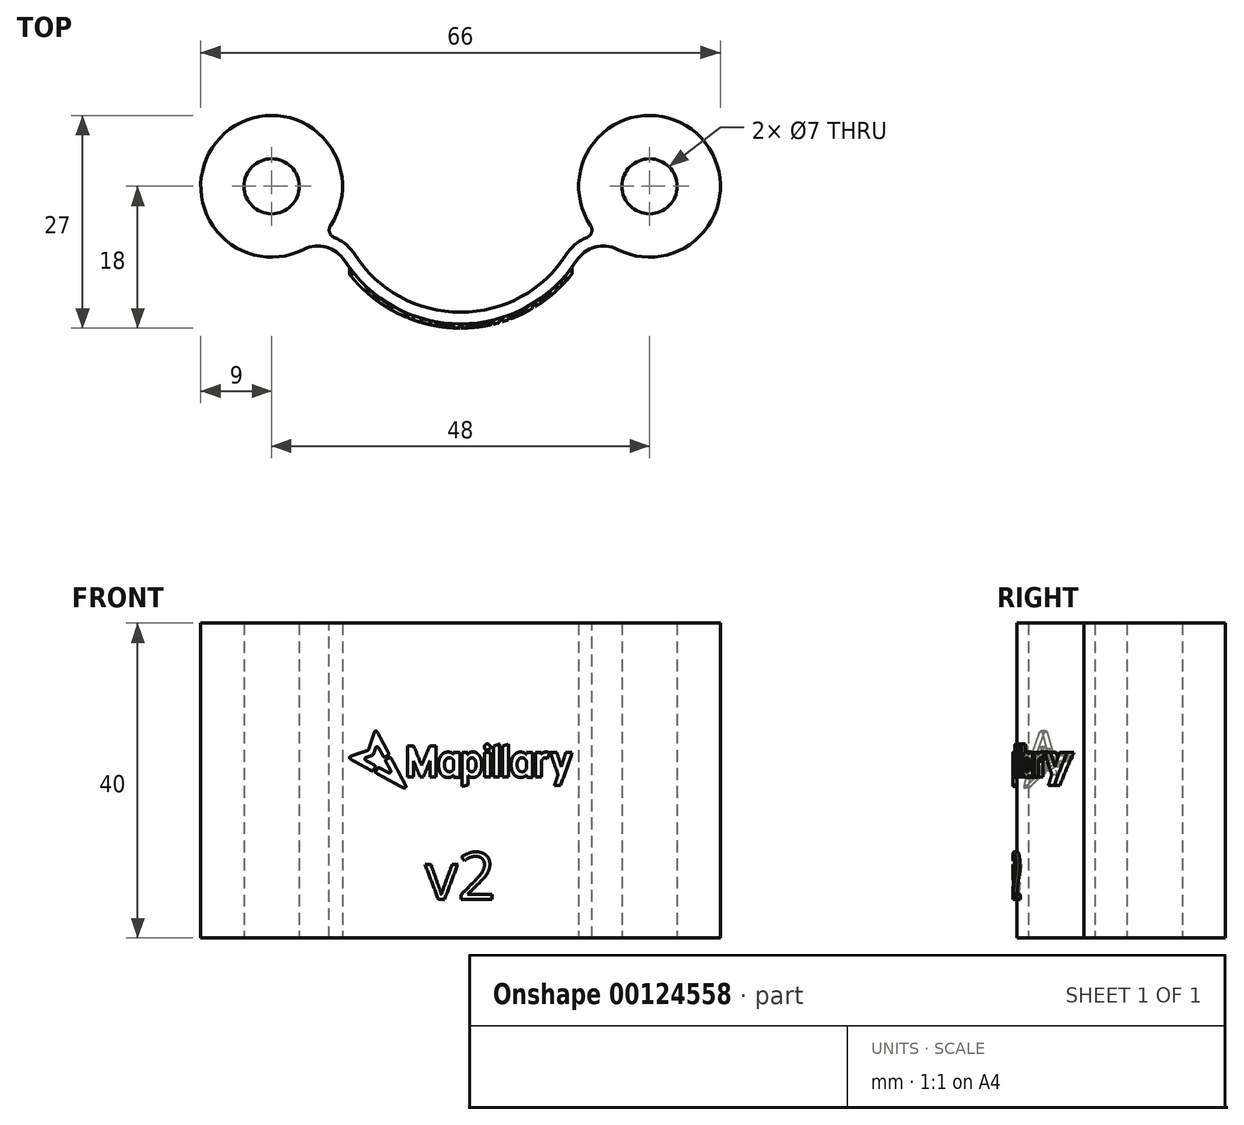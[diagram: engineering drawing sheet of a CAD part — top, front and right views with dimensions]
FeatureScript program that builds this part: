
annotation { "Feature Type Name" : "Feature", "Feature Type Description" : "" }
export const myFeature = defineFeature(function(context is Context, id is Id, definition is map)
    precondition{}
    {
        {
            var Q0;
            Q0=qCreatedBy(makeId("Top.planeOp"),FACE);
            var sketch = newSketch(context, id + "F0", { "sketchPlane" : qUnion([Q0])});
            skCircle(sketch, "E0", {"center": v(-24, 0) * mm, "radius": 3.5 * mm});
            skArc(sketch, "E1", {"start": v(-17.41, -6.13) * mm, "mid": v(-29.42, 7.19) * mm, "end": v(-19.92, -8.02) * mm});
            skArc(sketch, "E2", {"start": v(-13.48, -8.62) * mm, "mid": v(-7.68, -14.04) * mm, "end": v(0, -16) * mm});
            skArc(sketch, "E3", {"start": v(-14.74, -9.43) * mm, "mid": v(-8.4, -15.35) * mm, "end": v(0, -17.5) * mm});
            skArc(sketch, "E4", {"start": v(-14.74, -9.43) * mm, "mid": v(-17.06, -7.73) * mm, "end": v(-19.92, -8.02) * mm});
            skArc(sketch, "E5", {"start": v(-13.48, -8.62) * mm, "mid": v(-15.17, -6.94) * mm, "end": v(-17.41, -6.13) * mm});
            skArc(sketch, "E6.MirrorCS", {"start": v(14.74, -9.43) * mm, "mid": v(17.06, -7.73) * mm, "end": v(19.92, -8.02) * mm});
            skArc(sketch, "E7.MirrorCS", {"start": v(13.48, -8.62) * mm, "mid": v(15.17, -6.94) * mm, "end": v(17.41, -6.13) * mm});
            skCircle(sketch, "E8.MirrorC", {"center": v(24, 0) * mm, "radius": 3.5 * mm});
            skArc(sketch, "E9.MirrorCS", {"start": v(13.48, -8.62) * mm, "mid": v(7.68, -14.04) * mm, "end": v(0, -16) * mm});
            skArc(sketch, "E10.MirrorCS", {"start": v(17.41, -6.13) * mm, "mid": v(29.42, 7.19) * mm, "end": v(19.92, -8.02) * mm});
            skArc(sketch, "E11.MirrorCS", {"start": v(14.74, -9.43) * mm, "mid": v(8.4, -15.35) * mm, "end": v(0, -17.5) * mm});
            skSolve(sketch);
        }
        {
            var Q0;
            Q0 = qSketchRegion(id + "F0", true);
            extrude(context, id + "F1", {"entities" : qUnion([Q0]), "depth" : 40 * mm});
        }
        {
            var Q0;
            Q0=makeQuery(id+"F1.opExtrude","SWEPT_EDGE",EDGE,{"disambiguationData":[OSD([sQuery(id+"F0.wireOp",EDGE,"E1"),sQuery(id+"F0.wireOp",EDGE,"E5")])]});
            var Q1;
            Q1=makeQuery(id+"F1.opExtrude","SWEPT_EDGE",EDGE,{"disambiguationData":[OSD([sQuery(id+"F0.wireOp",EDGE,"E7.MirrorCS"),sQuery(id+"F0.wireOp",EDGE,"E10.MirrorCS")])]});
            fillet(context, id + "F2", {"entities" : qUnion([Q0, Q1]), "radius" : 1 * mm, "tangentPropagation" : true, "allowEdgeOverflow" : false});
        }
        {
            var Q0;
            Q0=qCreatedBy(makeId("Front.planeOp"),FACE);
            cPlane(context, id + "F3", {"entities" : qUnion([Q0]), "cplaneType" : CPlaneType.OFFSET, "offset" : 25 * mm, "width" : 150 * mm, "height" : 150 * mm});
        }
        {
            var Q0;
            Q0=qCreatedBy(id+"F3.planeOp",FACE);
            var sketch = newSketch(context, id + "F4", { "sketchPlane" : qUnion([Q0])});
            skLineSegment(sketch, "E12", {"start": v(-10.66, 20.91) * mm, "end": v(-10.64, 20.9) * mm});
            skLineSegment(sketch, "E13", {"start": v(-10.64, 20.9) * mm, "end": v(-10.6, 20.88) * mm});
            skLineSegment(sketch, "E14", {"start": v(-10.6, 20.88) * mm, "end": v(-10.55, 20.85) * mm});
            skLineSegment(sketch, "E15", {"start": v(-10.55, 20.85) * mm, "end": v(-10.48, 20.82) * mm});
            skLineSegment(sketch, "E16", {"start": v(-10.48, 20.82) * mm, "end": v(-10.4, 20.77) * mm});
            skLineSegment(sketch, "E17", {"start": v(-10.4, 20.77) * mm, "end": v(-10.3, 20.72) * mm});
            skLineSegment(sketch, "E18", {"start": v(-10.3, 20.72) * mm, "end": v(-10.2, 20.67) * mm});
            skLineSegment(sketch, "E19", {"start": v(-10.2, 20.67) * mm, "end": v(-10.09, 20.6) * mm});
            skLineSegment(sketch, "E20", {"start": v(-10.09, 20.6) * mm, "end": v(-9.97, 20.54) * mm});
            skLineSegment(sketch, "E21", {"start": v(-9.97, 20.54) * mm, "end": v(-9.84, 20.47) * mm});
            skLineSegment(sketch, "E22", {"start": v(-9.84, 20.47) * mm, "end": v(-9.7, 20.4) * mm});
            skLineSegment(sketch, "E23", {"start": v(-9.7, 20.4) * mm, "end": v(-9.56, 20.32) * mm});
            skLineSegment(sketch, "E24", {"start": v(-9.56, 20.32) * mm, "end": v(-9.41, 20.24) * mm});
            skLineSegment(sketch, "E25", {"start": v(-9.41, 20.24) * mm, "end": v(-9.26, 20.16) * mm});
            skLineSegment(sketch, "E26", {"start": v(-9.26, 20.16) * mm, "end": v(-9.1, 20.07) * mm});
            skLineSegment(sketch, "E27", {"start": v(-9.1, 20.07) * mm, "end": v(-8.96, 19.99) * mm});
            skLineSegment(sketch, "E28", {"start": v(-8.96, 19.99) * mm, "end": v(-8.8, 19.9) * mm});
            skLineSegment(sketch, "E29", {"start": v(-8.8, 19.9) * mm, "end": v(-8.65, 19.82) * mm});
            skLineSegment(sketch, "E30", {"start": v(-8.65, 19.82) * mm, "end": v(-8.5, 19.74) * mm});
            skLineSegment(sketch, "E31", {"start": v(-8.5, 19.74) * mm, "end": v(-8.36, 19.66) * mm});
            skLineSegment(sketch, "E32", {"start": v(-8.36, 19.66) * mm, "end": v(-8.22, 19.59) * mm});
            skLineSegment(sketch, "E33", {"start": v(-8.22, 19.59) * mm, "end": v(-8.08, 19.51) * mm});
            skLineSegment(sketch, "E34", {"start": v(-8.08, 19.51) * mm, "end": v(-7.95, 19.44) * mm});
            skLineSegment(sketch, "E35", {"start": v(-7.95, 19.44) * mm, "end": v(-7.83, 19.38) * mm});
            skLineSegment(sketch, "E36", {"start": v(-7.83, 19.38) * mm, "end": v(-7.72, 19.32) * mm});
            skLineSegment(sketch, "E37", {"start": v(-7.72, 19.32) * mm, "end": v(-7.62, 19.26) * mm});
            skLineSegment(sketch, "E38", {"start": v(-7.62, 19.26) * mm, "end": v(-7.52, 19.21) * mm});
            skLineSegment(sketch, "E39", {"start": v(-7.52, 19.21) * mm, "end": v(-7.45, 19.17) * mm});
            skLineSegment(sketch, "E40", {"start": v(-7.45, 19.17) * mm, "end": v(-7.38, 19.13) * mm});
            skLineSegment(sketch, "E41", {"start": v(-7.38, 19.13) * mm, "end": v(-7.33, 19.1) * mm});
            skLineSegment(sketch, "E42", {"start": v(-7.33, 19.1) * mm, "end": v(-7.3, 19.09) * mm});
            skLineSegment(sketch, "E43", {"start": v(-7.3, 19.09) * mm, "end": v(-7.28, 19.08) * mm});
            skLineSegment(sketch, "E44", {"start": v(-7.28, 19.08) * mm, "end": v(-7.2, 19.05) * mm});
            skLineSegment(sketch, "E45", {"start": v(-7.2, 19.05) * mm, "end": v(-7.13, 19.05) * mm});
            skLineSegment(sketch, "E46", {"start": v(-7.13, 19.05) * mm, "end": v(-7.07, 19.07) * mm});
            skLineSegment(sketch, "E47", {"start": v(-7.07, 19.07) * mm, "end": v(-7.01, 19.11) * mm});
            skLineSegment(sketch, "E48", {"start": v(-7.01, 19.11) * mm, "end": v(-6.97, 19.17) * mm});
            skLineSegment(sketch, "E49", {"start": v(-6.97, 19.17) * mm, "end": v(-6.95, 19.23) * mm});
            skLineSegment(sketch, "E50", {"start": v(-6.95, 19.23) * mm, "end": v(-6.95, 19.3) * mm});
            skLineSegment(sketch, "E51", {"start": v(-6.95, 19.3) * mm, "end": v(-6.98, 19.38) * mm});
            skLineSegment(sketch, "E52", {"start": v(-6.98, 19.38) * mm, "end": v(-6.99, 19.4) * mm});
            skLineSegment(sketch, "E53", {"start": v(-6.99, 19.4) * mm, "end": v(-7, 19.43) * mm});
            skLineSegment(sketch, "E54", {"start": v(-7, 19.43) * mm, "end": v(-7.03, 19.48) * mm});
            skLineSegment(sketch, "E55", {"start": v(-7.03, 19.48) * mm, "end": v(-7.07, 19.55) * mm});
            skLineSegment(sketch, "E56", {"start": v(-7.07, 19.55) * mm, "end": v(-7.11, 19.63) * mm});
            skLineSegment(sketch, "E57", {"start": v(-7.11, 19.63) * mm, "end": v(-7.16, 19.72) * mm});
            skLineSegment(sketch, "E58", {"start": v(-7.16, 19.72) * mm, "end": v(-7.22, 19.83) * mm});
            skLineSegment(sketch, "E59", {"start": v(-7.22, 19.83) * mm, "end": v(-7.28, 19.94) * mm});
            skLineSegment(sketch, "E60", {"start": v(-7.28, 19.94) * mm, "end": v(-7.34, 20.07) * mm});
            skLineSegment(sketch, "E61", {"start": v(-7.34, 20.07) * mm, "end": v(-7.41, 20.2) * mm});
            skLineSegment(sketch, "E62", {"start": v(-7.41, 20.2) * mm, "end": v(-7.48, 20.34) * mm});
            skLineSegment(sketch, "E63", {"start": v(-7.48, 20.34) * mm, "end": v(-7.56, 20.48) * mm});
            skLineSegment(sketch, "E64", {"start": v(-7.56, 20.48) * mm, "end": v(-7.64, 20.63) * mm});
            skLineSegment(sketch, "E65", {"start": v(-7.64, 20.63) * mm, "end": v(-7.72, 20.78) * mm});
            skLineSegment(sketch, "E66", {"start": v(-7.72, 20.78) * mm, "end": v(-7.8, 20.94) * mm});
            skLineSegment(sketch, "E67", {"start": v(-7.8, 20.94) * mm, "end": v(-7.88, 21.1) * mm});
            skLineSegment(sketch, "E68", {"start": v(-7.88, 21.1) * mm, "end": v(-7.97, 21.25) * mm});
            skLineSegment(sketch, "E69", {"start": v(-7.97, 21.25) * mm, "end": v(-8.05, 21.4) * mm});
            skLineSegment(sketch, "E70", {"start": v(-8.05, 21.4) * mm, "end": v(-8.13, 21.56) * mm});
            skLineSegment(sketch, "E71", {"start": v(-8.13, 21.56) * mm, "end": v(-8.2, 21.7) * mm});
            skLineSegment(sketch, "E72", {"start": v(-8.2, 21.7) * mm, "end": v(-8.29, 21.85) * mm});
            skLineSegment(sketch, "E73", {"start": v(-8.29, 21.85) * mm, "end": v(-8.36, 22) * mm});
            skLineSegment(sketch, "E74", {"start": v(-8.36, 22) * mm, "end": v(-8.43, 22.12) * mm});
            skLineSegment(sketch, "E75", {"start": v(-8.43, 22.12) * mm, "end": v(-8.5, 22.25) * mm});
            skLineSegment(sketch, "E76", {"start": v(-8.5, 22.25) * mm, "end": v(-8.56, 22.36) * mm});
            skLineSegment(sketch, "E77", {"start": v(-8.56, 22.36) * mm, "end": v(-8.61, 22.47) * mm});
            skLineSegment(sketch, "E78", {"start": v(-8.61, 22.47) * mm, "end": v(-8.66, 22.56) * mm});
            skLineSegment(sketch, "E79", {"start": v(-8.66, 22.56) * mm, "end": v(-8.7, 22.64) * mm});
            skLineSegment(sketch, "E80", {"start": v(-8.7, 22.64) * mm, "end": v(-8.74, 22.7) * mm});
            skLineSegment(sketch, "E81", {"start": v(-8.74, 22.7) * mm, "end": v(-8.77, 22.76) * mm});
            skLineSegment(sketch, "E82", {"start": v(-8.77, 22.76) * mm, "end": v(-8.79, 22.8) * mm});
            skLineSegment(sketch, "E83", {"start": v(-8.79, 22.8) * mm, "end": v(-8.8, 22.81) * mm});
            skLineSegment(sketch, "E84", {"start": v(-8.8, 22.81) * mm, "end": v(-8.85, 22.87) * mm});
            skLineSegment(sketch, "E85", {"start": v(-8.85, 22.87) * mm, "end": v(-8.93, 22.91) * mm});
            skLineSegment(sketch, "E86", {"start": v(-8.93, 22.91) * mm, "end": v(-9.02, 22.92) * mm});
            skLineSegment(sketch, "E87", {"start": v(-9.02, 22.92) * mm, "end": v(-9.1, 22.9) * mm});
            skLineSegment(sketch, "E88", {"start": v(-9.1, 22.9) * mm, "end": v(-9.18, 22.84) * mm});
            skLineSegment(sketch, "E89", {"start": v(-9.18, 22.84) * mm, "end": v(-9.26, 22.8) * mm});
            skLineSegment(sketch, "E90", {"start": v(-9.26, 22.8) * mm, "end": v(-9.33, 22.75) * mm});
            skLineSegment(sketch, "E91", {"start": v(-9.33, 22.75) * mm, "end": v(-9.4, 22.72) * mm});
            skLineSegment(sketch, "E92", {"start": v(-9.4, 22.72) * mm, "end": v(-9.47, 22.66) * mm});
            skLineSegment(sketch, "E93", {"start": v(-9.47, 22.66) * mm, "end": v(-9.51, 22.59) * mm});
            skLineSegment(sketch, "E94", {"start": v(-9.51, 22.59) * mm, "end": v(-9.52, 22.5) * mm});
            skLineSegment(sketch, "E95", {"start": v(-9.52, 22.5) * mm, "end": v(-9.48, 22.42) * mm});
            skLineSegment(sketch, "E96", {"start": v(-9.48, 22.42) * mm, "end": v(-9.46, 22.37) * mm});
            skLineSegment(sketch, "E97", {"start": v(-9.46, 22.37) * mm, "end": v(-9.42, 22.3) * mm});
            skLineSegment(sketch, "E98", {"start": v(-9.42, 22.3) * mm, "end": v(-9.38, 22.23) * mm});
            skLineSegment(sketch, "E99", {"start": v(-9.38, 22.23) * mm, "end": v(-9.34, 22.15) * mm});
            skLineSegment(sketch, "E100", {"start": v(-9.34, 22.15) * mm, "end": v(-9.3, 22.06) * mm});
            skLineSegment(sketch, "E101", {"start": v(-9.3, 22.06) * mm, "end": v(-9.25, 21.97) * mm});
            skLineSegment(sketch, "E102", {"start": v(-9.25, 21.97) * mm, "end": v(-9.2, 21.88) * mm});
            skLineSegment(sketch, "E103", {"start": v(-9.2, 21.88) * mm, "end": v(-9.15, 21.79) * mm});
            skLineSegment(sketch, "E104", {"start": v(-9.15, 21.79) * mm, "end": v(-9.1, 21.7) * mm});
            skLineSegment(sketch, "E105", {"start": v(-9.1, 21.7) * mm, "end": v(-9.06, 21.62) * mm});
            skLineSegment(sketch, "E106", {"start": v(-9.06, 21.62) * mm, "end": v(-9.02, 21.54) * mm});
            skLineSegment(sketch, "E107", {"start": v(-9.02, 21.54) * mm, "end": v(-8.98, 21.46) * mm});
            skLineSegment(sketch, "E108", {"start": v(-8.98, 21.46) * mm, "end": v(-8.94, 21.4) * mm});
            skLineSegment(sketch, "E109", {"start": v(-8.94, 21.4) * mm, "end": v(-8.92, 21.35) * mm});
            skLineSegment(sketch, "E110", {"start": v(-8.92, 21.35) * mm, "end": v(-8.9, 21.31) * mm});
            skLineSegment(sketch, "E111", {"start": v(-8.9, 21.31) * mm, "end": v(-8.88, 21.29) * mm});
            skLineSegment(sketch, "E112", {"start": v(-8.88, 21.29) * mm, "end": v(-8.86, 21.22) * mm});
            skLineSegment(sketch, "E113", {"start": v(-8.86, 21.22) * mm, "end": v(-8.86, 21.16) * mm});
            skLineSegment(sketch, "E114", {"start": v(-8.86, 21.16) * mm, "end": v(-8.88, 21.1) * mm});
            skLineSegment(sketch, "E115", {"start": v(-8.88, 21.1) * mm, "end": v(-8.92, 21.05) * mm});
            skLineSegment(sketch, "E116", {"start": v(-8.92, 21.05) * mm, "end": v(-8.98, 21.01) * mm});
            skLineSegment(sketch, "E117", {"start": v(-8.98, 21.01) * mm, "end": v(-9.04, 20.99) * mm});
            skLineSegment(sketch, "E118", {"start": v(-9.04, 20.99) * mm, "end": v(-9.1, 20.98) * mm});
            skLineSegment(sketch, "E119", {"start": v(-9.1, 20.98) * mm, "end": v(-9.16, 21) * mm});
            skLineSegment(sketch, "E120", {"start": v(-9.16, 21) * mm, "end": v(-9.18, 21.02) * mm});
            skLineSegment(sketch, "E121", {"start": v(-9.18, 21.02) * mm, "end": v(-9.22, 21.04) * mm});
            skLineSegment(sketch, "E122", {"start": v(-9.22, 21.04) * mm, "end": v(-9.28, 21.07) * mm});
            skLineSegment(sketch, "E123", {"start": v(-9.28, 21.07) * mm, "end": v(-9.35, 21.11) * mm});
            skLineSegment(sketch, "E124", {"start": v(-9.35, 21.11) * mm, "end": v(-9.44, 21.16) * mm});
            skLineSegment(sketch, "E125", {"start": v(-9.44, 21.16) * mm, "end": v(-9.53, 21.2) * mm});
            skLineSegment(sketch, "E126", {"start": v(-9.53, 21.2) * mm, "end": v(-9.62, 21.26) * mm});
            skLineSegment(sketch, "E127", {"start": v(-9.62, 21.26) * mm, "end": v(-9.72, 21.31) * mm});
            skLineSegment(sketch, "E128", {"start": v(-9.72, 21.31) * mm, "end": v(-9.82, 21.37) * mm});
            skLineSegment(sketch, "E129", {"start": v(-9.82, 21.37) * mm, "end": v(-9.92, 21.42) * mm});
            skLineSegment(sketch, "E130", {"start": v(-9.92, 21.42) * mm, "end": v(-10.01, 21.47) * mm});
            skLineSegment(sketch, "E131", {"start": v(-10.01, 21.47) * mm, "end": v(-10.1, 21.51) * mm});
            skLineSegment(sketch, "E132", {"start": v(-10.1, 21.51) * mm, "end": v(-10.17, 21.55) * mm});
            skLineSegment(sketch, "E133", {"start": v(-10.17, 21.55) * mm, "end": v(-10.23, 21.59) * mm});
            skLineSegment(sketch, "E134", {"start": v(-10.23, 21.59) * mm, "end": v(-10.27, 21.61) * mm});
            skLineSegment(sketch, "E135", {"start": v(-10.27, 21.61) * mm, "end": v(-10.3, 21.62) * mm});
            skLineSegment(sketch, "E136", {"start": v(-10.3, 21.62) * mm, "end": v(-10.36, 21.65) * mm});
            skLineSegment(sketch, "E137", {"start": v(-10.36, 21.65) * mm, "end": v(-10.43, 21.64) * mm});
            skLineSegment(sketch, "E138", {"start": v(-10.43, 21.64) * mm, "end": v(-10.5, 21.6) * mm});
            skLineSegment(sketch, "E139", {"start": v(-10.5, 21.6) * mm, "end": v(-10.58, 21.52) * mm});
            skLineSegment(sketch, "E140", {"start": v(-10.58, 21.52) * mm, "end": v(-10.62, 21.44) * mm});
            skLineSegment(sketch, "E141", {"start": v(-10.62, 21.44) * mm, "end": v(-10.67, 21.36) * mm});
            skLineSegment(sketch, "E142", {"start": v(-10.67, 21.36) * mm, "end": v(-10.72, 21.29) * mm});
            skLineSegment(sketch, "E143", {"start": v(-10.72, 21.29) * mm, "end": v(-10.75, 21.23) * mm});
            skLineSegment(sketch, "E144", {"start": v(-10.75, 21.23) * mm, "end": v(-10.78, 21.13) * mm});
            skLineSegment(sketch, "E145", {"start": v(-10.78, 21.13) * mm, "end": v(-10.78, 21.05) * mm});
            skLineSegment(sketch, "E146", {"start": v(-10.78, 21.05) * mm, "end": v(-10.74, 20.97) * mm});
            skLineSegment(sketch, "E147", {"start": v(-10.74, 20.97) * mm, "end": v(-10.66, 20.91) * mm});
            skLineSegment(sketch, "E148", {"start": v(-13.98, 22.72) * mm, "end": v(-14.04, 22.76) * mm});
            skLineSegment(sketch, "E149", {"start": v(-14.04, 22.76) * mm, "end": v(-14.07, 22.81) * mm});
            skLineSegment(sketch, "E150", {"start": v(-14.07, 22.81) * mm, "end": v(-14.1, 22.87) * mm});
            skLineSegment(sketch, "E151", {"start": v(-14.1, 22.87) * mm, "end": v(-14.09, 22.93) * mm});
            skLineSegment(sketch, "E152", {"start": v(-14.09, 22.93) * mm, "end": v(-14.07, 23) * mm});
            skLineSegment(sketch, "E153", {"start": v(-14.07, 23) * mm, "end": v(-14.03, 23.04) * mm});
            skLineSegment(sketch, "E154", {"start": v(-14.03, 23.04) * mm, "end": v(-13.98, 23.09) * mm});
            skLineSegment(sketch, "E155", {"start": v(-13.98, 23.09) * mm, "end": v(-13.9, 23.12) * mm});
            skLineSegment(sketch, "E156", {"start": v(-13.9, 23.12) * mm, "end": v(-13.86, 23.13) * mm});
            skLineSegment(sketch, "E157", {"start": v(-13.86, 23.13) * mm, "end": v(-13.79, 23.16) * mm});
            skLineSegment(sketch, "E158", {"start": v(-13.79, 23.16) * mm, "end": v(-13.69, 23.2) * mm});
            skLineSegment(sketch, "E159", {"start": v(-13.69, 23.2) * mm, "end": v(-13.57, 23.23) * mm});
            skLineSegment(sketch, "E160", {"start": v(-13.57, 23.23) * mm, "end": v(-13.44, 23.28) * mm});
            skLineSegment(sketch, "E161", {"start": v(-13.44, 23.28) * mm, "end": v(-13.3, 23.33) * mm});
            skLineSegment(sketch, "E162", {"start": v(-13.3, 23.33) * mm, "end": v(-13.13, 23.38) * mm});
            skLineSegment(sketch, "E163", {"start": v(-13.13, 23.38) * mm, "end": v(-12.97, 23.44) * mm});
            skLineSegment(sketch, "E164", {"start": v(-12.97, 23.44) * mm, "end": v(-12.8, 23.5) * mm});
            skLineSegment(sketch, "E165", {"start": v(-12.8, 23.5) * mm, "end": v(-12.64, 23.55) * mm});
            skLineSegment(sketch, "E166", {"start": v(-12.64, 23.55) * mm, "end": v(-12.47, 23.6) * mm});
            skLineSegment(sketch, "E167", {"start": v(-12.47, 23.6) * mm, "end": v(-12.32, 23.66) * mm});
            skLineSegment(sketch, "E168", {"start": v(-12.32, 23.66) * mm, "end": v(-12.17, 23.7) * mm});
            skLineSegment(sketch, "E169", {"start": v(-12.17, 23.7) * mm, "end": v(-12.04, 23.75) * mm});
            skLineSegment(sketch, "E170", {"start": v(-12.04, 23.75) * mm, "end": v(-11.93, 23.8) * mm});
            skLineSegment(sketch, "E171", {"start": v(-11.93, 23.8) * mm, "end": v(-11.83, 23.83) * mm});
            skLineSegment(sketch, "E172", {"start": v(-11.83, 23.83) * mm, "end": v(-11.78, 23.85) * mm});
            skLineSegment(sketch, "E173", {"start": v(-11.78, 23.85) * mm, "end": v(-11.73, 23.9) * mm});
            skLineSegment(sketch, "E174", {"start": v(-11.73, 23.9) * mm, "end": v(-11.7, 23.94) * mm});
            skLineSegment(sketch, "E175", {"start": v(-11.7, 23.94) * mm, "end": v(-11.67, 24) * mm});
            skLineSegment(sketch, "E176", {"start": v(-11.67, 24) * mm, "end": v(-11.63, 24.1) * mm});
            skLineSegment(sketch, "E177", {"start": v(-11.63, 24.1) * mm, "end": v(-11.6, 24.21) * mm});
            skLineSegment(sketch, "E178", {"start": v(-11.6, 24.21) * mm, "end": v(-11.55, 24.35) * mm});
            skLineSegment(sketch, "E179", {"start": v(-11.55, 24.35) * mm, "end": v(-11.5, 24.5) * mm});
            skLineSegment(sketch, "E180", {"start": v(-11.5, 24.5) * mm, "end": v(-11.45, 24.66) * mm});
            skLineSegment(sketch, "E181", {"start": v(-11.45, 24.66) * mm, "end": v(-11.4, 24.83) * mm});
            skLineSegment(sketch, "E182", {"start": v(-11.4, 24.83) * mm, "end": v(-11.33, 25) * mm});
            skLineSegment(sketch, "E183", {"start": v(-11.33, 25) * mm, "end": v(-11.28, 25.17) * mm});
            skLineSegment(sketch, "E184", {"start": v(-11.28, 25.17) * mm, "end": v(-11.22, 25.34) * mm});
            skLineSegment(sketch, "E185", {"start": v(-11.22, 25.34) * mm, "end": v(-11.17, 25.5) * mm});
            skLineSegment(sketch, "E186", {"start": v(-11.17, 25.5) * mm, "end": v(-11.12, 25.65) * mm});
            skLineSegment(sketch, "E187", {"start": v(-11.12, 25.65) * mm, "end": v(-11.07, 25.8) * mm});
            skLineSegment(sketch, "E188", {"start": v(-11.07, 25.8) * mm, "end": v(-11.03, 25.91) * mm});
            skLineSegment(sketch, "E189", {"start": v(-11.03, 25.91) * mm, "end": v(-11, 26) * mm});
            skLineSegment(sketch, "E190", {"start": v(-11, 26) * mm, "end": v(-10.97, 26.08) * mm});
            skLineSegment(sketch, "E191", {"start": v(-10.97, 26.08) * mm, "end": v(-10.96, 26.13) * mm});
            skLineSegment(sketch, "E192", {"start": v(-10.96, 26.13) * mm, "end": v(-10.93, 26.2) * mm});
            skLineSegment(sketch, "E193", {"start": v(-10.93, 26.2) * mm, "end": v(-10.88, 26.24) * mm});
            skLineSegment(sketch, "E194", {"start": v(-10.88, 26.24) * mm, "end": v(-10.83, 26.27) * mm});
            skLineSegment(sketch, "E195", {"start": v(-10.83, 26.27) * mm, "end": v(-10.77, 26.28) * mm});
            skLineSegment(sketch, "E196", {"start": v(-10.77, 26.28) * mm, "end": v(-10.7, 26.27) * mm});
            skLineSegment(sketch, "E197", {"start": v(-10.7, 26.27) * mm, "end": v(-10.65, 26.25) * mm});
            skLineSegment(sketch, "E198", {"start": v(-10.65, 26.25) * mm, "end": v(-10.6, 26.2) * mm});
            skLineSegment(sketch, "E199", {"start": v(-10.6, 26.2) * mm, "end": v(-10.55, 26.14) * mm});
            skLineSegment(sketch, "E200", {"start": v(-10.55, 26.14) * mm, "end": v(-10.53, 26.1) * mm});
            skLineSegment(sketch, "E201", {"start": v(-10.53, 26.1) * mm, "end": v(-10.49, 26.01) * mm});
            skLineSegment(sketch, "E202", {"start": v(-10.49, 26.01) * mm, "end": v(-10.42, 25.88) * mm});
            skLineSegment(sketch, "E203", {"start": v(-10.42, 25.88) * mm, "end": v(-10.33, 25.71) * mm});
            skLineSegment(sketch, "E204", {"start": v(-10.33, 25.71) * mm, "end": v(-10.22, 25.52) * mm});
            skLineSegment(sketch, "E205", {"start": v(-10.22, 25.52) * mm, "end": v(-10.1, 25.3) * mm});
            skLineSegment(sketch, "E206", {"start": v(-10.1, 25.3) * mm, "end": v(-9.99, 25.07) * mm});
            skLineSegment(sketch, "E207", {"start": v(-9.99, 25.07) * mm, "end": v(-9.86, 24.84) * mm});
            skLineSegment(sketch, "E208", {"start": v(-9.86, 24.84) * mm, "end": v(-9.73, 24.6) * mm});
            skLineSegment(sketch, "E209", {"start": v(-9.73, 24.6) * mm, "end": v(-9.6, 24.37) * mm});
            skLineSegment(sketch, "E210", {"start": v(-9.6, 24.37) * mm, "end": v(-9.5, 24.15) * mm});
            skLineSegment(sketch, "E211", {"start": v(-9.5, 24.15) * mm, "end": v(-9.39, 23.95) * mm});
            skLineSegment(sketch, "E212", {"start": v(-9.39, 23.95) * mm, "end": v(-9.3, 23.78) * mm});
            skLineSegment(sketch, "E213", {"start": v(-9.3, 23.78) * mm, "end": v(-9.23, 23.65) * mm});
            skLineSegment(sketch, "E214", {"start": v(-9.23, 23.65) * mm, "end": v(-9.18, 23.55) * mm});
            skLineSegment(sketch, "E215", {"start": v(-9.18, 23.55) * mm, "end": v(-9.15, 23.5) * mm});
            skLineSegment(sketch, "E216", {"start": v(-9.15, 23.5) * mm, "end": v(-9.13, 23.43) * mm});
            skLineSegment(sketch, "E217", {"start": v(-9.13, 23.43) * mm, "end": v(-9.14, 23.35) * mm});
            skLineSegment(sketch, "E218", {"start": v(-9.14, 23.35) * mm, "end": v(-9.18, 23.28) * mm});
            skLineSegment(sketch, "E219", {"start": v(-9.18, 23.28) * mm, "end": v(-9.24, 23.22) * mm});
            skLineSegment(sketch, "E220", {"start": v(-9.24, 23.22) * mm, "end": v(-9.33, 23.17) * mm});
            skLineSegment(sketch, "E221", {"start": v(-9.33, 23.17) * mm, "end": v(-9.43, 23.1) * mm});
            skLineSegment(sketch, "E222", {"start": v(-9.43, 23.1) * mm, "end": v(-9.51, 23.06) * mm});
            skLineSegment(sketch, "E223", {"start": v(-9.51, 23.06) * mm, "end": v(-9.58, 23.02) * mm});
            skLineSegment(sketch, "E224", {"start": v(-9.58, 23.02) * mm, "end": v(-9.65, 22.99) * mm});
            skLineSegment(sketch, "E225", {"start": v(-9.65, 22.99) * mm, "end": v(-9.73, 23) * mm});
            skLineSegment(sketch, "E226", {"start": v(-9.73, 23) * mm, "end": v(-9.79, 23.04) * mm});
            skLineSegment(sketch, "E227", {"start": v(-9.79, 23.04) * mm, "end": v(-9.83, 23.1) * mm});
            skLineSegment(sketch, "E228", {"start": v(-9.83, 23.1) * mm, "end": v(-9.87, 23.17) * mm});
            skLineSegment(sketch, "E229", {"start": v(-9.87, 23.17) * mm, "end": v(-9.92, 23.28) * mm});
            skLineSegment(sketch, "E230", {"start": v(-9.92, 23.28) * mm, "end": v(-10, 23.41) * mm});
            skLineSegment(sketch, "E231", {"start": v(-10, 23.41) * mm, "end": v(-10.08, 23.57) * mm});
            skLineSegment(sketch, "E232", {"start": v(-10.08, 23.57) * mm, "end": v(-10.17, 23.74) * mm});
            skLineSegment(sketch, "E233", {"start": v(-10.17, 23.74) * mm, "end": v(-10.26, 23.9) * mm});
            skLineSegment(sketch, "E234", {"start": v(-10.26, 23.9) * mm, "end": v(-10.35, 24.06) * mm});
            skLineSegment(sketch, "E235", {"start": v(-10.35, 24.06) * mm, "end": v(-10.41, 24.18) * mm});
            skLineSegment(sketch, "E236", {"start": v(-10.41, 24.18) * mm, "end": v(-10.45, 24.23) * mm});
            skLineSegment(sketch, "E237", {"start": v(-10.45, 24.23) * mm, "end": v(-10.5, 24.27) * mm});
            skLineSegment(sketch, "E238", {"start": v(-10.5, 24.27) * mm, "end": v(-10.55, 24.3) * mm});
            skLineSegment(sketch, "E239", {"start": v(-10.55, 24.3) * mm, "end": v(-10.6, 24.3) * mm});
            skLineSegment(sketch, "E240", {"start": v(-10.6, 24.3) * mm, "end": v(-10.66, 24.3) * mm});
            skLineSegment(sketch, "E241", {"start": v(-10.66, 24.3) * mm, "end": v(-10.72, 24.27) * mm});
            skLineSegment(sketch, "E242", {"start": v(-10.72, 24.27) * mm, "end": v(-10.76, 24.22) * mm});
            skLineSegment(sketch, "E243", {"start": v(-10.76, 24.22) * mm, "end": v(-10.8, 24.15) * mm});
            skLineSegment(sketch, "E244", {"start": v(-10.8, 24.15) * mm, "end": v(-10.82, 24.07) * mm});
            skLineSegment(sketch, "E245", {"start": v(-10.82, 24.07) * mm, "end": v(-10.85, 23.99) * mm});
            skLineSegment(sketch, "E246", {"start": v(-10.85, 23.99) * mm, "end": v(-10.88, 23.88) * mm});
            skLineSegment(sketch, "E247", {"start": v(-10.88, 23.88) * mm, "end": v(-10.92, 23.78) * mm});
            skLineSegment(sketch, "E248", {"start": v(-10.92, 23.78) * mm, "end": v(-10.96, 23.67) * mm});
            skLineSegment(sketch, "E249", {"start": v(-10.96, 23.67) * mm, "end": v(-11, 23.56) * mm});
            skLineSegment(sketch, "E250", {"start": v(-11, 23.56) * mm, "end": v(-11.02, 23.46) * mm});
            skLineSegment(sketch, "E251", {"start": v(-11.02, 23.46) * mm, "end": v(-11.05, 23.38) * mm});
            skLineSegment(sketch, "E252", {"start": v(-11.05, 23.38) * mm, "end": v(-11.08, 23.32) * mm});
            skLineSegment(sketch, "E253", {"start": v(-11.08, 23.32) * mm, "end": v(-11.12, 23.27) * mm});
            skLineSegment(sketch, "E254", {"start": v(-11.12, 23.27) * mm, "end": v(-11.17, 23.23) * mm});
            skLineSegment(sketch, "E255", {"start": v(-11.17, 23.23) * mm, "end": v(-11.22, 23.2) * mm});
            skLineSegment(sketch, "E256", {"start": v(-11.22, 23.2) * mm, "end": v(-11.3, 23.18) * mm});
            skLineSegment(sketch, "E257", {"start": v(-11.3, 23.18) * mm, "end": v(-11.4, 23.15) * mm});
            skLineSegment(sketch, "E258", {"start": v(-11.4, 23.15) * mm, "end": v(-11.5, 23.11) * mm});
            skLineSegment(sketch, "E259", {"start": v(-11.5, 23.11) * mm, "end": v(-11.6, 23.08) * mm});
            skLineSegment(sketch, "E260", {"start": v(-11.6, 23.08) * mm, "end": v(-11.7, 23.04) * mm});
            skLineSegment(sketch, "E261", {"start": v(-11.7, 23.04) * mm, "end": v(-11.8, 23) * mm});
            skLineSegment(sketch, "E262", {"start": v(-11.8, 23) * mm, "end": v(-11.9, 22.97) * mm});
            skLineSegment(sketch, "E263", {"start": v(-11.9, 22.97) * mm, "end": v(-11.99, 22.94) * mm});
            skLineSegment(sketch, "E264", {"start": v(-11.99, 22.94) * mm, "end": v(-12.04, 22.92) * mm});
            skLineSegment(sketch, "E265", {"start": v(-12.04, 22.92) * mm, "end": v(-12.09, 22.88) * mm});
            skLineSegment(sketch, "E266", {"start": v(-12.09, 22.88) * mm, "end": v(-12.12, 22.82) * mm});
            skLineSegment(sketch, "E267", {"start": v(-12.12, 22.82) * mm, "end": v(-12.13, 22.77) * mm});
            skLineSegment(sketch, "E268", {"start": v(-12.13, 22.77) * mm, "end": v(-12.13, 22.7) * mm});
            skLineSegment(sketch, "E269", {"start": v(-12.13, 22.7) * mm, "end": v(-12.11, 22.65) * mm});
            skLineSegment(sketch, "E270", {"start": v(-12.11, 22.65) * mm, "end": v(-12.07, 22.6) * mm});
            skLineSegment(sketch, "E271", {"start": v(-12.07, 22.6) * mm, "end": v(-12.01, 22.55) * mm});
            skLineSegment(sketch, "E272", {"start": v(-12.01, 22.55) * mm, "end": v(-12, 22.54) * mm});
            skLineSegment(sketch, "E273", {"start": v(-12, 22.54) * mm, "end": v(-11.96, 22.52) * mm});
            skLineSegment(sketch, "E274", {"start": v(-11.96, 22.52) * mm, "end": v(-11.9, 22.5) * mm});
            skLineSegment(sketch, "E275", {"start": v(-11.9, 22.5) * mm, "end": v(-11.84, 22.46) * mm});
            skLineSegment(sketch, "E276", {"start": v(-11.84, 22.46) * mm, "end": v(-11.76, 22.42) * mm});
            skLineSegment(sketch, "E277", {"start": v(-11.76, 22.42) * mm, "end": v(-11.68, 22.37) * mm});
            skLineSegment(sketch, "E278", {"start": v(-11.68, 22.37) * mm, "end": v(-11.6, 22.33) * mm});
            skLineSegment(sketch, "E279", {"start": v(-11.6, 22.33) * mm, "end": v(-11.5, 22.27) * mm});
            skLineSegment(sketch, "E280", {"start": v(-11.5, 22.27) * mm, "end": v(-11.4, 22.22) * mm});
            skLineSegment(sketch, "E281", {"start": v(-11.4, 22.22) * mm, "end": v(-11.32, 22.17) * mm});
            skLineSegment(sketch, "E282", {"start": v(-11.32, 22.17) * mm, "end": v(-11.23, 22.13) * mm});
            skLineSegment(sketch, "E283", {"start": v(-11.23, 22.13) * mm, "end": v(-11.15, 22.08) * mm});
            skLineSegment(sketch, "E284", {"start": v(-11.15, 22.08) * mm, "end": v(-11.08, 22.05) * mm});
            skLineSegment(sketch, "E285", {"start": v(-11.08, 22.05) * mm, "end": v(-11.02, 22.01) * mm});
            skLineSegment(sketch, "E286", {"start": v(-11.02, 22.01) * mm, "end": v(-10.98, 22) * mm});
            skLineSegment(sketch, "E287", {"start": v(-10.98, 22) * mm, "end": v(-10.95, 21.98) * mm});
            skLineSegment(sketch, "E288", {"start": v(-10.95, 21.98) * mm, "end": v(-10.89, 21.93) * mm});
            skLineSegment(sketch, "E289", {"start": v(-10.89, 21.93) * mm, "end": v(-10.85, 21.86) * mm});
            skLineSegment(sketch, "E290", {"start": v(-10.85, 21.86) * mm, "end": v(-10.84, 21.78) * mm});
            skLineSegment(sketch, "E291", {"start": v(-10.84, 21.78) * mm, "end": v(-10.86, 21.7) * mm});
            skLineSegment(sketch, "E292", {"start": v(-10.86, 21.7) * mm, "end": v(-10.92, 21.6) * mm});
            skLineSegment(sketch, "E293", {"start": v(-10.92, 21.6) * mm, "end": v(-10.98, 21.5) * mm});
            skLineSegment(sketch, "E294", {"start": v(-10.98, 21.5) * mm, "end": v(-11.03, 21.41) * mm});
            skLineSegment(sketch, "E295", {"start": v(-11.03, 21.41) * mm, "end": v(-11.07, 21.35) * mm});
            skLineSegment(sketch, "E296", {"start": v(-11.07, 21.35) * mm, "end": v(-11.12, 21.3) * mm});
            skLineSegment(sketch, "E297", {"start": v(-11.12, 21.3) * mm, "end": v(-11.2, 21.26) * mm});
            skLineSegment(sketch, "E298", {"start": v(-11.2, 21.26) * mm, "end": v(-11.27, 21.26) * mm});
            skLineSegment(sketch, "E299", {"start": v(-11.27, 21.26) * mm, "end": v(-11.35, 21.28) * mm});
            skLineSegment(sketch, "E300", {"start": v(-11.35, 21.28) * mm, "end": v(-11.37, 21.3) * mm});
            skLineSegment(sketch, "E301", {"start": v(-11.37, 21.3) * mm, "end": v(-11.4, 21.3) * mm});
            skLineSegment(sketch, "E302", {"start": v(-11.4, 21.3) * mm, "end": v(-11.44, 21.33) * mm});
            skLineSegment(sketch, "E303", {"start": v(-11.44, 21.33) * mm, "end": v(-11.49, 21.36) * mm});
            skLineSegment(sketch, "E304", {"start": v(-11.49, 21.36) * mm, "end": v(-11.55, 21.4) * mm});
            skLineSegment(sketch, "E305", {"start": v(-11.55, 21.4) * mm, "end": v(-11.62, 21.43) * mm});
            skLineSegment(sketch, "E306", {"start": v(-11.62, 21.43) * mm, "end": v(-11.7, 21.48) * mm});
            skLineSegment(sketch, "E307", {"start": v(-11.7, 21.48) * mm, "end": v(-11.8, 21.53) * mm});
            skLineSegment(sketch, "E308", {"start": v(-11.8, 21.53) * mm, "end": v(-11.9, 21.58) * mm});
            skLineSegment(sketch, "E309", {"start": v(-11.9, 21.58) * mm, "end": v(-12, 21.64) * mm});
            skLineSegment(sketch, "E310", {"start": v(-12, 21.64) * mm, "end": v(-12.1, 21.7) * mm});
            skLineSegment(sketch, "E311", {"start": v(-12.1, 21.7) * mm, "end": v(-12.21, 21.75) * mm});
            skLineSegment(sketch, "E312", {"start": v(-12.21, 21.75) * mm, "end": v(-12.33, 21.82) * mm});
            skLineSegment(sketch, "E313", {"start": v(-12.33, 21.82) * mm, "end": v(-12.44, 21.88) * mm});
            skLineSegment(sketch, "E314", {"start": v(-12.44, 21.88) * mm, "end": v(-12.56, 21.95) * mm});
            skLineSegment(sketch, "E315", {"start": v(-12.56, 21.95) * mm, "end": v(-12.68, 22.01) * mm});
            skLineSegment(sketch, "E316", {"start": v(-12.68, 22.01) * mm, "end": v(-12.8, 22.08) * mm});
            skLineSegment(sketch, "E317", {"start": v(-12.8, 22.08) * mm, "end": v(-12.92, 22.14) * mm});
            skLineSegment(sketch, "E318", {"start": v(-12.92, 22.14) * mm, "end": v(-13.04, 22.2) * mm});
            skLineSegment(sketch, "E319", {"start": v(-13.04, 22.2) * mm, "end": v(-13.15, 22.27) * mm});
            skLineSegment(sketch, "E320", {"start": v(-13.15, 22.27) * mm, "end": v(-13.26, 22.33) * mm});
            skLineSegment(sketch, "E321", {"start": v(-13.26, 22.33) * mm, "end": v(-13.37, 22.38) * mm});
            skLineSegment(sketch, "E322", {"start": v(-13.37, 22.38) * mm, "end": v(-13.47, 22.44) * mm});
            skLineSegment(sketch, "E323", {"start": v(-13.47, 22.44) * mm, "end": v(-13.56, 22.5) * mm});
            skLineSegment(sketch, "E324", {"start": v(-13.56, 22.5) * mm, "end": v(-13.65, 22.54) * mm});
            skLineSegment(sketch, "E325", {"start": v(-13.65, 22.54) * mm, "end": v(-13.73, 22.58) * mm});
            skLineSegment(sketch, "E326", {"start": v(-13.73, 22.58) * mm, "end": v(-13.8, 22.62) * mm});
            skLineSegment(sketch, "E327", {"start": v(-13.8, 22.62) * mm, "end": v(-13.86, 22.65) * mm});
            skLineSegment(sketch, "E328", {"start": v(-13.86, 22.65) * mm, "end": v(-13.9, 22.68) * mm});
            skLineSegment(sketch, "E329", {"start": v(-13.9, 22.68) * mm, "end": v(-13.95, 22.7) * mm});
            skLineSegment(sketch, "E330", {"start": v(-13.95, 22.7) * mm, "end": v(-13.97, 22.71) * mm});
            skLineSegment(sketch, "E331", {"start": v(-13.97, 22.71) * mm, "end": v(-13.98, 22.72) * mm});
            skLineSegment(sketch, "E332", {"start": v(-3.11, 24.43) * mm, "end": v(-3.11, 20.47) * mm});
            skLineSegment(sketch, "E333", {"start": v(-3.11, 20.47) * mm, "end": v(-3.87, 20.47) * mm});
            skLineSegment(sketch, "E334", {"start": v(-3.87, 20.47) * mm, "end": v(-3.87, 22.53) * mm});
            skLineSegment(sketch, "E335", {"start": v(-3.87, 22.53) * mm, "end": v(-4.73, 20.47) * mm});
            skLineSegment(sketch, "E336", {"start": v(-4.73, 20.47) * mm, "end": v(-5.14, 20.47) * mm});
            skLineSegment(sketch, "E337", {"start": v(-5.14, 20.47) * mm, "end": v(-6, 22.53) * mm});
            skLineSegment(sketch, "E338", {"start": v(-6, 22.53) * mm, "end": v(-6, 20.47) * mm});
            skLineSegment(sketch, "E339", {"start": v(-6, 20.47) * mm, "end": v(-6.76, 20.47) * mm});
            skLineSegment(sketch, "E340", {"start": v(-6.76, 20.47) * mm, "end": v(-6.76, 24.43) * mm});
            skLineSegment(sketch, "E341", {"start": v(-6.76, 24.43) * mm, "end": v(-5.98, 24.43) * mm});
            skLineSegment(sketch, "E342", {"start": v(-5.98, 24.43) * mm, "end": v(-4.94, 21.94) * mm});
            skLineSegment(sketch, "E343", {"start": v(-4.94, 21.94) * mm, "end": v(-3.9, 24.43) * mm});
            skLineSegment(sketch, "E344", {"start": v(-3.9, 24.43) * mm, "end": v(-3.11, 24.43) * mm});
            skLineSegment(sketch, "E345", {"start": v(0.2, 23.57) * mm, "end": v(0.88, 23.57) * mm});
            skLineSegment(sketch, "E346", {"start": v(0.88, 23.57) * mm, "end": v(0.88, 23.3) * mm});
            skLineSegment(sketch, "E347", {"start": v(0.88, 23.3) * mm, "end": v(0.92, 23.38) * mm});
            skLineSegment(sketch, "E348", {"start": v(0.92, 23.38) * mm, "end": v(0.98, 23.44) * mm});
            skLineSegment(sketch, "E349", {"start": v(0.98, 23.44) * mm, "end": v(1.05, 23.5) * mm});
            skLineSegment(sketch, "E350", {"start": v(1.05, 23.5) * mm, "end": v(1.14, 23.54) * mm});
            skLineSegment(sketch, "E351", {"start": v(1.14, 23.54) * mm, "end": v(1.36, 23.62) * mm});
            skLineSegment(sketch, "E352", {"start": v(1.36, 23.62) * mm, "end": v(1.59, 23.64) * mm});
            skLineSegment(sketch, "E353", {"start": v(1.59, 23.64) * mm, "end": v(1.8, 23.62) * mm});
            skLineSegment(sketch, "E354", {"start": v(1.8, 23.62) * mm, "end": v(2.02, 23.54) * mm});
            skLineSegment(sketch, "E355", {"start": v(2.02, 23.54) * mm, "end": v(2.2, 23.4) * mm});
            skLineSegment(sketch, "E356", {"start": v(2.2, 23.4) * mm, "end": v(2.37, 23.22) * mm});
            skLineSegment(sketch, "E357", {"start": v(2.37, 23.22) * mm, "end": v(2.5, 23) * mm});
            skLineSegment(sketch, "E358", {"start": v(2.5, 23) * mm, "end": v(2.6, 22.71) * mm});
            skLineSegment(sketch, "E359", {"start": v(2.6, 22.71) * mm, "end": v(2.67, 22.39) * mm});
            skLineSegment(sketch, "E360", {"start": v(2.67, 22.39) * mm, "end": v(2.69, 22.02) * mm});
            skLineSegment(sketch, "E361", {"start": v(2.69, 22.02) * mm, "end": v(2.68, 21.83) * mm});
            skLineSegment(sketch, "E362", {"start": v(2.68, 21.83) * mm, "end": v(2.67, 21.65) * mm});
            skLineSegment(sketch, "E363", {"start": v(2.67, 21.65) * mm, "end": v(2.64, 21.48) * mm});
            skLineSegment(sketch, "E364", {"start": v(2.64, 21.48) * mm, "end": v(2.6, 21.32) * mm});
            skLineSegment(sketch, "E365", {"start": v(2.6, 21.32) * mm, "end": v(2.5, 21.04) * mm});
            skLineSegment(sketch, "E366", {"start": v(2.5, 21.04) * mm, "end": v(2.38, 20.8) * mm});
            skLineSegment(sketch, "E367", {"start": v(2.38, 20.8) * mm, "end": v(2.22, 20.63) * mm});
            skLineSegment(sketch, "E368", {"start": v(2.22, 20.63) * mm, "end": v(2.03, 20.5) * mm});
            skLineSegment(sketch, "E369", {"start": v(2.03, 20.5) * mm, "end": v(1.82, 20.42) * mm});
            skLineSegment(sketch, "E370", {"start": v(1.82, 20.42) * mm, "end": v(1.6, 20.4) * mm});
            skLineSegment(sketch, "E371", {"start": v(1.6, 20.4) * mm, "end": v(1.48, 20.4) * mm});
            skLineSegment(sketch, "E372", {"start": v(1.48, 20.4) * mm, "end": v(1.37, 20.42) * mm});
            skLineSegment(sketch, "E373", {"start": v(1.37, 20.42) * mm, "end": v(1.27, 20.44) * mm});
            skLineSegment(sketch, "E374", {"start": v(1.27, 20.44) * mm, "end": v(1.2, 20.48) * mm});
            skLineSegment(sketch, "E375", {"start": v(1.2, 20.48) * mm, "end": v(1.06, 20.57) * mm});
            skLineSegment(sketch, "E376", {"start": v(1.06, 20.57) * mm, "end": v(0.97, 20.68) * mm});
            skLineSegment(sketch, "E377", {"start": v(0.97, 20.68) * mm, "end": v(0.97, 19.44) * mm});
            skLineSegment(sketch, "E378", {"start": v(0.97, 19.44) * mm, "end": v(0.2, 19.28) * mm});
            skLineSegment(sketch, "E379", {"start": v(0.2, 19.28) * mm, "end": v(0.2, 23.57) * mm});
            skLineSegment(sketch, "E380", {"start": v(1.4, 21.14) * mm, "end": v(1.54, 21.15) * mm});
            skLineSegment(sketch, "E381", {"start": v(1.54, 21.15) * mm, "end": v(1.65, 21.2) * mm});
            skLineSegment(sketch, "E382", {"start": v(1.65, 21.2) * mm, "end": v(1.74, 21.26) * mm});
            skLineSegment(sketch, "E383", {"start": v(1.74, 21.26) * mm, "end": v(1.82, 21.36) * mm});
            skLineSegment(sketch, "E384", {"start": v(1.82, 21.36) * mm, "end": v(1.88, 21.48) * mm});
            skLineSegment(sketch, "E385", {"start": v(1.88, 21.48) * mm, "end": v(1.93, 21.63) * mm});
            skLineSegment(sketch, "E386", {"start": v(1.93, 21.63) * mm, "end": v(1.95, 21.8) * mm});
            skLineSegment(sketch, "E387", {"start": v(1.95, 21.8) * mm, "end": v(1.96, 22.02) * mm});
            skLineSegment(sketch, "E388", {"start": v(1.96, 22.02) * mm, "end": v(1.95, 22.22) * mm});
            skLineSegment(sketch, "E389", {"start": v(1.95, 22.22) * mm, "end": v(1.93, 22.4) * mm});
            skLineSegment(sketch, "E390", {"start": v(1.93, 22.4) * mm, "end": v(1.88, 22.54) * mm});
            skLineSegment(sketch, "E391", {"start": v(1.88, 22.54) * mm, "end": v(1.82, 22.67) * mm});
            skLineSegment(sketch, "E392", {"start": v(1.82, 22.67) * mm, "end": v(1.75, 22.77) * mm});
            skLineSegment(sketch, "E393", {"start": v(1.75, 22.77) * mm, "end": v(1.66, 22.84) * mm});
            skLineSegment(sketch, "E394", {"start": v(1.66, 22.84) * mm, "end": v(1.55, 22.88) * mm});
            skLineSegment(sketch, "E395", {"start": v(1.55, 22.88) * mm, "end": v(1.43, 22.9) * mm});
            skLineSegment(sketch, "E396", {"start": v(1.43, 22.9) * mm, "end": v(1.34, 22.88) * mm});
            skLineSegment(sketch, "E397", {"start": v(1.34, 22.88) * mm, "end": v(1.26, 22.86) * mm});
            skLineSegment(sketch, "E398", {"start": v(1.26, 22.86) * mm, "end": v(1.18, 22.82) * mm});
            skLineSegment(sketch, "E399", {"start": v(1.18, 22.82) * mm, "end": v(1.11, 22.76) * mm});
            skLineSegment(sketch, "E400", {"start": v(1.11, 22.76) * mm, "end": v(1, 22.61) * mm});
            skLineSegment(sketch, "E401", {"start": v(1, 22.61) * mm, "end": v(0.92, 22.44) * mm});
            skLineSegment(sketch, "E402", {"start": v(0.92, 22.44) * mm, "end": v(0.92, 21.56) * mm});
            skLineSegment(sketch, "E403", {"start": v(0.92, 21.56) * mm, "end": v(1.01, 21.37) * mm});
            skLineSegment(sketch, "E404", {"start": v(1.01, 21.37) * mm, "end": v(1.13, 21.24) * mm});
            skLineSegment(sketch, "E405", {"start": v(1.13, 21.24) * mm, "end": v(1.27, 21.16) * mm});
            skLineSegment(sketch, "E406", {"start": v(1.27, 21.16) * mm, "end": v(1.4, 21.14) * mm});
            skLineSegment(sketch, "E407", {"start": v(3.79, 23.57) * mm, "end": v(3.79, 20.47) * mm});
            skLineSegment(sketch, "E408", {"start": v(3.79, 20.47) * mm, "end": v(3.02, 20.47) * mm});
            skLineSegment(sketch, "E409", {"start": v(3.02, 20.47) * mm, "end": v(3.02, 23.57) * mm});
            skLineSegment(sketch, "E410", {"start": v(3.02, 23.57) * mm, "end": v(3.79, 23.57) * mm});
            skLineSegment(sketch, "E411", {"start": v(3.02, 24.25) * mm, "end": v(3.05, 24.4) * mm});
            skLineSegment(sketch, "E412", {"start": v(3.05, 24.4) * mm, "end": v(3.12, 24.54) * mm});
            skLineSegment(sketch, "E413", {"start": v(3.12, 24.54) * mm, "end": v(3.18, 24.6) * mm});
            skLineSegment(sketch, "E414", {"start": v(3.18, 24.6) * mm, "end": v(3.25, 24.63) * mm});
            skLineSegment(sketch, "E415", {"start": v(3.25, 24.63) * mm, "end": v(3.32, 24.65) * mm});
            skLineSegment(sketch, "E416", {"start": v(3.32, 24.65) * mm, "end": v(3.4, 24.66) * mm});
            skLineSegment(sketch, "E417", {"start": v(3.4, 24.66) * mm, "end": v(3.55, 24.63) * mm});
            skLineSegment(sketch, "E418", {"start": v(3.55, 24.63) * mm, "end": v(3.67, 24.54) * mm});
            skLineSegment(sketch, "E419", {"start": v(3.67, 24.54) * mm, "end": v(3.76, 24.4) * mm});
            skLineSegment(sketch, "E420", {"start": v(3.76, 24.4) * mm, "end": v(3.79, 24.25) * mm});
            skLineSegment(sketch, "E421", {"start": v(3.79, 24.25) * mm, "end": v(3.76, 24.1) * mm});
            skLineSegment(sketch, "E422", {"start": v(3.76, 24.1) * mm, "end": v(3.67, 23.98) * mm});
            skLineSegment(sketch, "E423", {"start": v(3.67, 23.98) * mm, "end": v(3.55, 23.9) * mm});
            skLineSegment(sketch, "E424", {"start": v(3.55, 23.9) * mm, "end": v(3.4, 23.87) * mm});
            skLineSegment(sketch, "E425", {"start": v(3.4, 23.87) * mm, "end": v(3.32, 23.88) * mm});
            skLineSegment(sketch, "E426", {"start": v(3.32, 23.88) * mm, "end": v(3.25, 23.9) * mm});
            skLineSegment(sketch, "E427", {"start": v(3.25, 23.9) * mm, "end": v(3.18, 23.93) * mm});
            skLineSegment(sketch, "E428", {"start": v(3.18, 23.93) * mm, "end": v(3.12, 23.98) * mm});
            skLineSegment(sketch, "E429", {"start": v(3.12, 23.98) * mm, "end": v(3.05, 24.1) * mm});
            skLineSegment(sketch, "E430", {"start": v(3.05, 24.1) * mm, "end": v(3.02, 24.25) * mm});
            skLineSegment(sketch, "E431", {"start": v(4.18, 24.38) * mm, "end": v(4.94, 24.64) * mm});
            skLineSegment(sketch, "E432", {"start": v(4.94, 24.64) * mm, "end": v(4.94, 20.47) * mm});
            skLineSegment(sketch, "E433", {"start": v(4.94, 20.47) * mm, "end": v(4.18, 20.47) * mm});
            skLineSegment(sketch, "E434", {"start": v(4.18, 20.47) * mm, "end": v(4.18, 24.38) * mm});
            skLineSegment(sketch, "E435", {"start": v(5.34, 24.38) * mm, "end": v(6.1, 24.64) * mm});
            skLineSegment(sketch, "E436", {"start": v(6.1, 24.64) * mm, "end": v(6.1, 20.47) * mm});
            skLineSegment(sketch, "E437", {"start": v(6.1, 20.47) * mm, "end": v(5.34, 20.47) * mm});
            skLineSegment(sketch, "E438", {"start": v(5.34, 20.47) * mm, "end": v(5.34, 24.38) * mm});
            skLineSegment(sketch, "E439", {"start": v(10.23, 23.57) * mm, "end": v(10.23, 23.36) * mm});
            skLineSegment(sketch, "E440", {"start": v(10.23, 23.36) * mm, "end": v(10.34, 23.47) * mm});
            skLineSegment(sketch, "E441", {"start": v(10.34, 23.47) * mm, "end": v(10.49, 23.56) * mm});
            skLineSegment(sketch, "E442", {"start": v(10.49, 23.56) * mm, "end": v(10.67, 23.62) * mm});
            skLineSegment(sketch, "E443", {"start": v(10.67, 23.62) * mm, "end": v(10.86, 23.64) * mm});
            skLineSegment(sketch, "E444", {"start": v(10.86, 23.64) * mm, "end": v(11, 23.63) * mm});
            skLineSegment(sketch, "E445", {"start": v(11, 23.63) * mm, "end": v(11.11, 23.6) * mm});
            skLineSegment(sketch, "E446", {"start": v(11.11, 23.6) * mm, "end": v(11.22, 23.55) * mm});
            skLineSegment(sketch, "E447", {"start": v(11.22, 23.55) * mm, "end": v(11.3, 23.47) * mm});
            skLineSegment(sketch, "E448", {"start": v(11.3, 23.47) * mm, "end": v(11.03, 22.78) * mm});
            skLineSegment(sketch, "E449", {"start": v(11.03, 22.78) * mm, "end": v(10.88, 22.87) * mm});
            skLineSegment(sketch, "E450", {"start": v(10.88, 22.87) * mm, "end": v(10.72, 22.9) * mm});
            skLineSegment(sketch, "E451", {"start": v(10.72, 22.9) * mm, "end": v(10.58, 22.88) * mm});
            skLineSegment(sketch, "E452", {"start": v(10.58, 22.88) * mm, "end": v(10.46, 22.8) * mm});
            skLineSegment(sketch, "E453", {"start": v(10.46, 22.8) * mm, "end": v(10.36, 22.66) * mm});
            skLineSegment(sketch, "E454", {"start": v(10.36, 22.66) * mm, "end": v(10.28, 22.47) * mm});
            skLineSegment(sketch, "E455", {"start": v(10.28, 22.47) * mm, "end": v(10.28, 20.47) * mm});
            skLineSegment(sketch, "E456", {"start": v(10.28, 20.47) * mm, "end": v(9.52, 20.47) * mm});
            skLineSegment(sketch, "E457", {"start": v(9.52, 20.47) * mm, "end": v(9.52, 23.57) * mm});
            skLineSegment(sketch, "E458", {"start": v(9.52, 23.57) * mm, "end": v(10.23, 23.57) * mm});
            skLineSegment(sketch, "E459", {"start": v(8.35, 20.7) * mm, "end": v(8.2, 20.57) * mm});
            skLineSegment(sketch, "E460", {"start": v(8.2, 20.57) * mm, "end": v(8.03, 20.48) * mm});
            skLineSegment(sketch, "E461", {"start": v(8.03, 20.48) * mm, "end": v(7.85, 20.41) * mm});
            skLineSegment(sketch, "E462", {"start": v(7.85, 20.41) * mm, "end": v(7.66, 20.4) * mm});
            skLineSegment(sketch, "E463", {"start": v(7.66, 20.4) * mm, "end": v(7.5, 20.4) * mm});
            skLineSegment(sketch, "E464", {"start": v(7.5, 20.4) * mm, "end": v(7.36, 20.42) * mm});
            skLineSegment(sketch, "E465", {"start": v(7.36, 20.42) * mm, "end": v(7.22, 20.46) * mm});
            skLineSegment(sketch, "E466", {"start": v(7.22, 20.46) * mm, "end": v(7.1, 20.52) * mm});
            skLineSegment(sketch, "E467", {"start": v(7.1, 20.52) * mm, "end": v(6.99, 20.59) * mm});
            skLineSegment(sketch, "E468", {"start": v(6.99, 20.59) * mm, "end": v(6.89, 20.67) * mm});
            skLineSegment(sketch, "E469", {"start": v(6.89, 20.67) * mm, "end": v(6.8, 20.76) * mm});
            skLineSegment(sketch, "E470", {"start": v(6.8, 20.76) * mm, "end": v(6.72, 20.87) * mm});
            skLineSegment(sketch, "E471", {"start": v(6.72, 20.87) * mm, "end": v(6.65, 20.98) * mm});
            skLineSegment(sketch, "E472", {"start": v(6.65, 20.98) * mm, "end": v(6.59, 21.1) * mm});
            skLineSegment(sketch, "E473", {"start": v(6.59, 21.1) * mm, "end": v(6.54, 21.24) * mm});
            skLineSegment(sketch, "E474", {"start": v(6.54, 21.24) * mm, "end": v(6.5, 21.38) * mm});
            skLineSegment(sketch, "E475", {"start": v(6.5, 21.38) * mm, "end": v(6.46, 21.53) * mm});
            skLineSegment(sketch, "E476", {"start": v(6.46, 21.53) * mm, "end": v(6.44, 21.68) * mm});
            skLineSegment(sketch, "E477", {"start": v(6.44, 21.68) * mm, "end": v(6.43, 21.85) * mm});
            skLineSegment(sketch, "E478", {"start": v(6.43, 21.85) * mm, "end": v(6.42, 22.01) * mm});
            skLineSegment(sketch, "E479", {"start": v(6.42, 22.01) * mm, "end": v(6.43, 22.18) * mm});
            skLineSegment(sketch, "E480", {"start": v(6.43, 22.18) * mm, "end": v(6.44, 22.34) * mm});
            skLineSegment(sketch, "E481", {"start": v(6.44, 22.34) * mm, "end": v(6.46, 22.5) * mm});
            skLineSegment(sketch, "E482", {"start": v(6.46, 22.5) * mm, "end": v(6.5, 22.64) * mm});
            skLineSegment(sketch, "E483", {"start": v(6.5, 22.64) * mm, "end": v(6.54, 22.78) * mm});
            skLineSegment(sketch, "E484", {"start": v(6.54, 22.78) * mm, "end": v(6.59, 22.92) * mm});
            skLineSegment(sketch, "E485", {"start": v(6.59, 22.92) * mm, "end": v(6.65, 23.04) * mm});
            skLineSegment(sketch, "E486", {"start": v(6.65, 23.04) * mm, "end": v(6.72, 23.16) * mm});
            skLineSegment(sketch, "E487", {"start": v(6.72, 23.16) * mm, "end": v(6.8, 23.26) * mm});
            skLineSegment(sketch, "E488", {"start": v(6.8, 23.26) * mm, "end": v(6.89, 23.35) * mm});
            skLineSegment(sketch, "E489", {"start": v(6.89, 23.35) * mm, "end": v(6.99, 23.44) * mm});
            skLineSegment(sketch, "E490", {"start": v(6.99, 23.44) * mm, "end": v(7.1, 23.5) * mm});
            skLineSegment(sketch, "E491", {"start": v(7.1, 23.5) * mm, "end": v(7.22, 23.56) * mm});
            skLineSegment(sketch, "E492", {"start": v(7.22, 23.56) * mm, "end": v(7.36, 23.6) * mm});
            skLineSegment(sketch, "E493", {"start": v(7.36, 23.6) * mm, "end": v(7.5, 23.62) * mm});
            skLineSegment(sketch, "E494", {"start": v(7.5, 23.62) * mm, "end": v(7.66, 23.63) * mm});
            skLineSegment(sketch, "E495", {"start": v(7.66, 23.63) * mm, "end": v(7.86, 23.6) * mm});
            skLineSegment(sketch, "E496", {"start": v(7.86, 23.6) * mm, "end": v(8.04, 23.55) * mm});
            skLineSegment(sketch, "E497", {"start": v(8.04, 23.55) * mm, "end": v(8.2, 23.46) * mm});
            skLineSegment(sketch, "E498", {"start": v(8.2, 23.46) * mm, "end": v(8.35, 23.34) * mm});
            skLineSegment(sketch, "E499", {"start": v(8.35, 23.34) * mm, "end": v(8.35, 23.59) * mm});
            skLineSegment(sketch, "E500", {"start": v(8.35, 23.59) * mm, "end": v(9.13, 23.59) * mm});
            skLineSegment(sketch, "E501", {"start": v(9.13, 23.59) * mm, "end": v(9.13, 20.43) * mm});
            skLineSegment(sketch, "E502", {"start": v(9.13, 20.43) * mm, "end": v(8.35, 20.43) * mm});
            skLineSegment(sketch, "E503", {"start": v(8.35, 20.43) * mm, "end": v(8.35, 20.7) * mm});
            skLineSegment(sketch, "E504", {"start": v(8.35, 21.48) * mm, "end": v(8.27, 21.33) * mm});
            skLineSegment(sketch, "E505", {"start": v(8.27, 21.33) * mm, "end": v(8.15, 21.22) * mm});
            skLineSegment(sketch, "E506", {"start": v(8.15, 21.22) * mm, "end": v(8, 21.15) * mm});
            skLineSegment(sketch, "E507", {"start": v(8, 21.15) * mm, "end": v(7.84, 21.13) * mm});
            skLineSegment(sketch, "E508", {"start": v(7.84, 21.13) * mm, "end": v(7.67, 21.14) * mm});
            skLineSegment(sketch, "E509", {"start": v(7.67, 21.14) * mm, "end": v(7.54, 21.19) * mm});
            skLineSegment(sketch, "E510", {"start": v(7.54, 21.19) * mm, "end": v(7.43, 21.27) * mm});
            skLineSegment(sketch, "E511", {"start": v(7.43, 21.27) * mm, "end": v(7.34, 21.38) * mm});
            skLineSegment(sketch, "E512", {"start": v(7.34, 21.38) * mm, "end": v(7.27, 21.5) * mm});
            skLineSegment(sketch, "E513", {"start": v(7.27, 21.5) * mm, "end": v(7.22, 21.66) * mm});
            skLineSegment(sketch, "E514", {"start": v(7.22, 21.66) * mm, "end": v(7.2, 21.82) * mm});
            skLineSegment(sketch, "E515", {"start": v(7.2, 21.82) * mm, "end": v(7.18, 22) * mm});
            skLineSegment(sketch, "E516", {"start": v(7.18, 22) * mm, "end": v(7.18, 22.18) * mm});
            skLineSegment(sketch, "E517", {"start": v(7.18, 22.18) * mm, "end": v(7.2, 22.35) * mm});
            skLineSegment(sketch, "E518", {"start": v(7.2, 22.35) * mm, "end": v(7.25, 22.5) * mm});
            skLineSegment(sketch, "E519", {"start": v(7.25, 22.5) * mm, "end": v(7.31, 22.63) * mm});
            skLineSegment(sketch, "E520", {"start": v(7.31, 22.63) * mm, "end": v(7.4, 22.74) * mm});
            skLineSegment(sketch, "E521", {"start": v(7.4, 22.74) * mm, "end": v(7.5, 22.83) * mm});
            skLineSegment(sketch, "E522", {"start": v(7.5, 22.83) * mm, "end": v(7.64, 22.88) * mm});
            skLineSegment(sketch, "E523", {"start": v(7.64, 22.88) * mm, "end": v(7.8, 22.9) * mm});
            skLineSegment(sketch, "E524", {"start": v(7.8, 22.9) * mm, "end": v(7.9, 22.9) * mm});
            skLineSegment(sketch, "E525", {"start": v(7.9, 22.9) * mm, "end": v(7.98, 22.88) * mm});
            skLineSegment(sketch, "E526", {"start": v(7.98, 22.88) * mm, "end": v(8.06, 22.84) * mm});
            skLineSegment(sketch, "E527", {"start": v(8.06, 22.84) * mm, "end": v(8.13, 22.8) * mm});
            skLineSegment(sketch, "E528", {"start": v(8.13, 22.8) * mm, "end": v(8.2, 22.74) * mm});
            skLineSegment(sketch, "E529", {"start": v(8.2, 22.74) * mm, "end": v(8.26, 22.67) * mm});
            skLineSegment(sketch, "E530", {"start": v(8.26, 22.67) * mm, "end": v(8.3, 22.59) * mm});
            skLineSegment(sketch, "E531", {"start": v(8.3, 22.59) * mm, "end": v(8.35, 22.5) * mm});
            skLineSegment(sketch, "E532", {"start": v(8.35, 22.5) * mm, "end": v(8.35, 21.48) * mm});
            skLineSegment(sketch, "E533", {"start": v(-0.87, 20.7) * mm, "end": v(-1.02, 20.57) * mm});
            skLineSegment(sketch, "E534", {"start": v(-1.02, 20.57) * mm, "end": v(-1.2, 20.48) * mm});
            skLineSegment(sketch, "E535", {"start": v(-1.2, 20.48) * mm, "end": v(-1.37, 20.41) * mm});
            skLineSegment(sketch, "E536", {"start": v(-1.37, 20.41) * mm, "end": v(-1.56, 20.4) * mm});
            skLineSegment(sketch, "E537", {"start": v(-1.56, 20.4) * mm, "end": v(-1.72, 20.4) * mm});
            skLineSegment(sketch, "E538", {"start": v(-1.72, 20.4) * mm, "end": v(-1.86, 20.42) * mm});
            skLineSegment(sketch, "E539", {"start": v(-1.86, 20.42) * mm, "end": v(-2, 20.46) * mm});
            skLineSegment(sketch, "E540", {"start": v(-2, 20.46) * mm, "end": v(-2.12, 20.52) * mm});
            skLineSegment(sketch, "E541", {"start": v(-2.12, 20.52) * mm, "end": v(-2.23, 20.59) * mm});
            skLineSegment(sketch, "E542", {"start": v(-2.23, 20.59) * mm, "end": v(-2.33, 20.67) * mm});
            skLineSegment(sketch, "E543", {"start": v(-2.33, 20.67) * mm, "end": v(-2.42, 20.76) * mm});
            skLineSegment(sketch, "E544", {"start": v(-2.42, 20.76) * mm, "end": v(-2.5, 20.87) * mm});
            skLineSegment(sketch, "E545", {"start": v(-2.5, 20.87) * mm, "end": v(-2.57, 20.98) * mm});
            skLineSegment(sketch, "E546", {"start": v(-2.57, 20.98) * mm, "end": v(-2.64, 21.1) * mm});
            skLineSegment(sketch, "E547", {"start": v(-2.64, 21.1) * mm, "end": v(-2.69, 21.24) * mm});
            skLineSegment(sketch, "E548", {"start": v(-2.69, 21.24) * mm, "end": v(-2.73, 21.38) * mm});
            skLineSegment(sketch, "E549", {"start": v(-2.73, 21.38) * mm, "end": v(-2.76, 21.53) * mm});
            skLineSegment(sketch, "E550", {"start": v(-2.76, 21.53) * mm, "end": v(-2.78, 21.68) * mm});
            skLineSegment(sketch, "E551", {"start": v(-2.78, 21.68) * mm, "end": v(-2.8, 21.85) * mm});
            skLineSegment(sketch, "E552", {"start": v(-2.8, 21.85) * mm, "end": v(-2.8, 22.01) * mm});
            skLineSegment(sketch, "E553", {"start": v(-2.8, 22.01) * mm, "end": v(-2.8, 22.18) * mm});
            skLineSegment(sketch, "E554", {"start": v(-2.8, 22.18) * mm, "end": v(-2.78, 22.34) * mm});
            skLineSegment(sketch, "E555", {"start": v(-2.78, 22.34) * mm, "end": v(-2.76, 22.5) * mm});
            skLineSegment(sketch, "E556", {"start": v(-2.76, 22.5) * mm, "end": v(-2.73, 22.64) * mm});
            skLineSegment(sketch, "E557", {"start": v(-2.73, 22.64) * mm, "end": v(-2.69, 22.78) * mm});
            skLineSegment(sketch, "E558", {"start": v(-2.69, 22.78) * mm, "end": v(-2.64, 22.92) * mm});
            skLineSegment(sketch, "E559", {"start": v(-2.64, 22.92) * mm, "end": v(-2.57, 23.04) * mm});
            skLineSegment(sketch, "E560", {"start": v(-2.57, 23.04) * mm, "end": v(-2.5, 23.16) * mm});
            skLineSegment(sketch, "E561", {"start": v(-2.5, 23.16) * mm, "end": v(-2.42, 23.26) * mm});
            skLineSegment(sketch, "E562", {"start": v(-2.42, 23.26) * mm, "end": v(-2.33, 23.35) * mm});
            skLineSegment(sketch, "E563", {"start": v(-2.33, 23.35) * mm, "end": v(-2.23, 23.44) * mm});
            skLineSegment(sketch, "E564", {"start": v(-2.23, 23.44) * mm, "end": v(-2.12, 23.5) * mm});
            skLineSegment(sketch, "E565", {"start": v(-2.12, 23.5) * mm, "end": v(-2, 23.56) * mm});
            skLineSegment(sketch, "E566", {"start": v(-2, 23.56) * mm, "end": v(-1.86, 23.6) * mm});
            skLineSegment(sketch, "E567", {"start": v(-1.86, 23.6) * mm, "end": v(-1.72, 23.62) * mm});
            skLineSegment(sketch, "E568", {"start": v(-1.72, 23.62) * mm, "end": v(-1.56, 23.63) * mm});
            skLineSegment(sketch, "E569", {"start": v(-1.56, 23.63) * mm, "end": v(-1.36, 23.6) * mm});
            skLineSegment(sketch, "E570", {"start": v(-1.36, 23.6) * mm, "end": v(-1.18, 23.55) * mm});
            skLineSegment(sketch, "E571", {"start": v(-1.18, 23.55) * mm, "end": v(-1.02, 23.46) * mm});
            skLineSegment(sketch, "E572", {"start": v(-1.02, 23.46) * mm, "end": v(-0.87, 23.34) * mm});
            skLineSegment(sketch, "E573", {"start": v(-0.87, 23.34) * mm, "end": v(-0.87, 23.59) * mm});
            skLineSegment(sketch, "E574", {"start": v(-0.87, 23.59) * mm, "end": v(-0.1, 23.59) * mm});
            skLineSegment(sketch, "E575", {"start": v(-0.1, 23.59) * mm, "end": v(-0.1, 20.43) * mm});
            skLineSegment(sketch, "E576", {"start": v(-0.1, 20.43) * mm, "end": v(-0.87, 20.43) * mm});
            skLineSegment(sketch, "E577", {"start": v(-0.87, 20.43) * mm, "end": v(-0.87, 20.7) * mm});
            skLineSegment(sketch, "E578", {"start": v(-0.87, 21.48) * mm, "end": v(-0.95, 21.33) * mm});
            skLineSegment(sketch, "E579", {"start": v(-0.95, 21.33) * mm, "end": v(-1.07, 21.22) * mm});
            skLineSegment(sketch, "E580", {"start": v(-1.07, 21.22) * mm, "end": v(-1.21, 21.15) * mm});
            skLineSegment(sketch, "E581", {"start": v(-1.21, 21.15) * mm, "end": v(-1.38, 21.13) * mm});
            skLineSegment(sketch, "E582", {"start": v(-1.38, 21.13) * mm, "end": v(-1.55, 21.14) * mm});
            skLineSegment(sketch, "E583", {"start": v(-1.55, 21.14) * mm, "end": v(-1.68, 21.19) * mm});
            skLineSegment(sketch, "E584", {"start": v(-1.68, 21.19) * mm, "end": v(-1.8, 21.27) * mm});
            skLineSegment(sketch, "E585", {"start": v(-1.8, 21.27) * mm, "end": v(-1.88, 21.38) * mm});
            skLineSegment(sketch, "E586", {"start": v(-1.88, 21.38) * mm, "end": v(-1.95, 21.5) * mm});
            skLineSegment(sketch, "E587", {"start": v(-1.95, 21.5) * mm, "end": v(-2, 21.66) * mm});
            skLineSegment(sketch, "E588", {"start": v(-2, 21.66) * mm, "end": v(-2.03, 21.82) * mm});
            skLineSegment(sketch, "E589", {"start": v(-2.03, 21.82) * mm, "end": v(-2.04, 22) * mm});
            skLineSegment(sketch, "E590", {"start": v(-2.04, 22) * mm, "end": v(-2.04, 22.18) * mm});
            skLineSegment(sketch, "E591", {"start": v(-2.04, 22.18) * mm, "end": v(-2.01, 22.35) * mm});
            skLineSegment(sketch, "E592", {"start": v(-2.01, 22.35) * mm, "end": v(-1.97, 22.5) * mm});
            skLineSegment(sketch, "E593", {"start": v(-1.97, 22.5) * mm, "end": v(-1.9, 22.63) * mm});
            skLineSegment(sketch, "E594", {"start": v(-1.9, 22.63) * mm, "end": v(-1.82, 22.74) * mm});
            skLineSegment(sketch, "E595", {"start": v(-1.82, 22.74) * mm, "end": v(-1.71, 22.83) * mm});
            skLineSegment(sketch, "E596", {"start": v(-1.71, 22.83) * mm, "end": v(-1.58, 22.88) * mm});
            skLineSegment(sketch, "E597", {"start": v(-1.58, 22.88) * mm, "end": v(-1.41, 22.9) * mm});
            skLineSegment(sketch, "E598", {"start": v(-1.41, 22.9) * mm, "end": v(-1.33, 22.9) * mm});
            skLineSegment(sketch, "E599", {"start": v(-1.33, 22.9) * mm, "end": v(-1.24, 22.88) * mm});
            skLineSegment(sketch, "E600", {"start": v(-1.24, 22.88) * mm, "end": v(-1.16, 22.84) * mm});
            skLineSegment(sketch, "E601", {"start": v(-1.16, 22.84) * mm, "end": v(-1.1, 22.8) * mm});
            skLineSegment(sketch, "E602", {"start": v(-1.1, 22.8) * mm, "end": v(-1.02, 22.74) * mm});
            skLineSegment(sketch, "E603", {"start": v(-1.02, 22.74) * mm, "end": v(-0.96, 22.67) * mm});
            skLineSegment(sketch, "E604", {"start": v(-0.96, 22.67) * mm, "end": v(-0.91, 22.59) * mm});
            skLineSegment(sketch, "E605", {"start": v(-0.91, 22.59) * mm, "end": v(-0.87, 22.5) * mm});
            skLineSegment(sketch, "E606", {"start": v(-0.87, 22.5) * mm, "end": v(-0.87, 21.48) * mm});
            skLineSegment(sketch, "E607", {"start": v(12.7, 19.37) * mm, "end": v(11.91, 19.37) * mm});
            skLineSegment(sketch, "E608", {"start": v(11.91, 19.37) * mm, "end": v(12.39, 20.74) * mm});
            skLineSegment(sketch, "E609", {"start": v(12.39, 20.74) * mm, "end": v(11.39, 23.57) * mm});
            skLineSegment(sketch, "E610", {"start": v(11.39, 23.57) * mm, "end": v(12.23, 23.57) * mm});
            skLineSegment(sketch, "E611", {"start": v(12.23, 23.57) * mm, "end": v(12.8, 21.77) * mm});
            skLineSegment(sketch, "E612", {"start": v(12.8, 21.77) * mm, "end": v(13.36, 23.57) * mm});
            skLineSegment(sketch, "E613", {"start": v(13.36, 23.57) * mm, "end": v(14.18, 23.57) * mm});
            skLineSegment(sketch, "E614", {"start": v(14.18, 23.57) * mm, "end": v(12.7, 19.37) * mm});
            skLineSegment(sketch, "E615", {"start": v(-14.2, -26.25) * mm, "end": v(-14.2, -26.26) * mm});
            skLineSegment(sketch, "E616", {"start": v(-14.2, -26.26) * mm, "end": v(-14.21, -26.27) * mm});
            skLineSegment(sketch, "E617", {"start": v(-14.21, -26.27) * mm, "end": v(-14.23, -26.28) * mm});
            skLineSegment(sketch, "E618", {"start": v(-14.23, -26.28) * mm, "end": v(-14.24, -26.28) * mm});
            skLineSegment(sketch, "E619", {"start": v(-14.24, -26.28) * mm, "end": v(-14.25, -26.28) * mm});
            skLineSegment(sketch, "E620", {"start": v(-14.25, -26.28) * mm, "end": v(-14.26, -26.27) * mm});
            skLineSegment(sketch, "E621", {"start": v(-14.26, -26.27) * mm, "end": v(-14.27, -26.26) * mm});
            skLineSegment(sketch, "E622", {"start": v(-14.27, -26.26) * mm, "end": v(-14.27, -26.25) * mm});
            skLineSegment(sketch, "E623", {"start": v(-14.27, -26.25) * mm, "end": v(-14.27, -26.24) * mm});
            skLineSegment(sketch, "E624", {"start": v(-14.27, -26.24) * mm, "end": v(-14.26, -26.23) * mm});
            skLineSegment(sketch, "E625", {"start": v(-14.26, -26.23) * mm, "end": v(-14.25, -26.22) * mm});
            skLineSegment(sketch, "E626", {"start": v(-14.25, -26.22) * mm, "end": v(-14.24, -26.22) * mm});
            skLineSegment(sketch, "E627", {"start": v(-14.24, -26.22) * mm, "end": v(-14.23, -26.22) * mm});
            skLineSegment(sketch, "E628", {"start": v(-14.23, -26.22) * mm, "end": v(-14.21, -26.23) * mm});
            skLineSegment(sketch, "E629", {"start": v(-14.21, -26.23) * mm, "end": v(-14.2, -26.24) * mm});
            skLineSegment(sketch, "E630", {"start": v(-14.2, -26.24) * mm, "end": v(-14.2, -26.25) * mm});
            skLineSegment(sketch, "E631", {"start": v(14.27, -26.25) * mm, "end": v(14.27, -26.26) * mm});
            skLineSegment(sketch, "E632", {"start": v(14.27, -26.26) * mm, "end": v(14.27, -26.27) * mm});
            skLineSegment(sketch, "E633", {"start": v(14.27, -26.27) * mm, "end": v(14.26, -26.28) * mm});
            skLineSegment(sketch, "E634", {"start": v(14.26, -26.28) * mm, "end": v(14.24, -26.28) * mm});
            skLineSegment(sketch, "E635", {"start": v(14.24, -26.28) * mm, "end": v(14.23, -26.28) * mm});
            skLineSegment(sketch, "E636", {"start": v(14.23, -26.28) * mm, "end": v(14.22, -26.27) * mm});
            skLineSegment(sketch, "E637", {"start": v(14.22, -26.27) * mm, "end": v(14.21, -26.26) * mm});
            skLineSegment(sketch, "E638", {"start": v(14.21, -26.26) * mm, "end": v(14.21, -26.25) * mm});
            skLineSegment(sketch, "E639", {"start": v(14.21, -26.25) * mm, "end": v(14.21, -26.24) * mm});
            skLineSegment(sketch, "E640", {"start": v(14.21, -26.24) * mm, "end": v(14.22, -26.22) * mm});
            skLineSegment(sketch, "E641", {"start": v(14.22, -26.22) * mm, "end": v(14.23, -26.22) * mm});
            skLineSegment(sketch, "E642", {"start": v(14.23, -26.22) * mm, "end": v(14.24, -26.21) * mm});
            skLineSegment(sketch, "E643", {"start": v(14.24, -26.21) * mm, "end": v(14.25, -26.22) * mm});
            skLineSegment(sketch, "E644", {"start": v(14.25, -26.22) * mm, "end": v(14.27, -26.22) * mm});
            skLineSegment(sketch, "E645", {"start": v(14.27, -26.22) * mm, "end": v(14.27, -26.23) * mm});
            skLineSegment(sketch, "E646", {"start": v(14.27, -26.23) * mm, "end": v(14.27, -26.25) * mm});
            skText(sketch, "E647", { "text": "v2", "fontName": "OpenSans-Regular.ttf"});
            const initialGuessF4  = {"E647": [-0.00452, 0.00492, 1, 0, 0.006]};
            skSetInitialGuess(sketch, initialGuessF4);
            skSolve(sketch);
        }
        {
            var Q0;
            Q0 = qSketchRegion(id + "F4", true);
            extrude(context, id + "F5", {"entities" : qUnion([Q0]), "operationType" : NewBodyOperationType.ADD, "oppositeDirection" : true, "depth" : 25 * mm});
        }
        {
            var Q0;
            Q0=qCreatedBy(makeId("Top.planeOp"),FACE);
            var sketch = newSketch(context, id + "F6", { "sketchPlane" : qUnion([Q0])});
            skArc(sketch, "E648.0", {"start": v(-15.16, -9.7) * mm, "mid": v(-17.2, -8.21) * mm, "end": v(-19.7, -8.47) * mm});
            skArc(sketch, "E648.1", {"start": v(-15.16, -9.7) * mm, "mid": v(0, -18) * mm, "end": v(15.16, -9.7) * mm});
            skArc(sketch, "E648.2", {"start": v(15.16, -9.7) * mm, "mid": v(17.2, -8.21) * mm, "end": v(19.7, -8.47) * mm});
            skArc(sketch, "E649.0", {"start": v(-16.52, -5) * mm, "mid": v(-29.97, 6.73) * mm, "end": v(-19.92, -8.02) * mm});
            skArc(sketch, "E649.1", {"start": v(16.52, -5) * mm, "mid": v(29.97, 6.73) * mm, "end": v(19.92, -8.02) * mm});
            skArc(sketch, "E649.2", {"start": v(13.48, -8.62) * mm, "mid": v(14.6, -7.35) * mm, "end": v(16.06, -6.49) * mm});
            skArc(sketch, "E649.3", {"start": v(13.48, -8.62) * mm, "mid": v(0, -16) * mm, "end": v(-13.48, -8.62) * mm});
            skArc(sketch, "E649.4", {"start": v(-13.48, -8.62) * mm, "mid": v(-14.6, -7.35) * mm, "end": v(-16.06, -6.49) * mm});
            skPoint(sketch, "E650.visualSharp", {"position": v(-17.41, -6.13) * mm});
            skArc(sketch, "E650.filletArc", {"start": v(-16.52, -5) * mm, "mid": v(-16.64, -5.85) * mm, "end": v(-16.06, -6.49) * mm});
            skPoint(sketch, "E651.visualSharp", {"position": v(17.41, -6.13) * mm});
            skArc(sketch, "E651.filletArc", {"start": v(16.06, -6.49) * mm, "mid": v(16.64, -5.85) * mm, "end": v(16.52, -5) * mm});
            skLineSegment(sketch, "E652", {"start": v(-19.7, -8.47) * mm, "end": v(-19.92, -8.02) * mm});
            skLineSegment(sketch, "E653", {"start": v(19.7, -8.47) * mm, "end": v(19.92, -8.02) * mm});
            skLineSegment(sketch, "E654.bottom", {"start": v(-43.93, -25) * mm, "end": v(43.93, -25) * mm});
            skLineSegment(sketch, "E654.top", {"start": v(-43.93, 20.53) * mm, "end": v(43.93, 20.53) * mm});
            skLineSegment(sketch, "E654.left", {"start": v(-43.93, -25) * mm, "end": v(-43.93, 20.53) * mm});
            skLineSegment(sketch, "E654.right", {"start": v(43.93, -25) * mm, "end": v(43.93, 20.53) * mm});
            skSolve(sketch);
        }
        {
            var Q0;
            Q0 = qSketchRegion(id + "F6", true);
            extrude(context, id + "F7", {"entities" : qUnion([Q0]), "operationType" : NewBodyOperationType.REMOVE, "depth" : 60 * mm});
        }
    });
